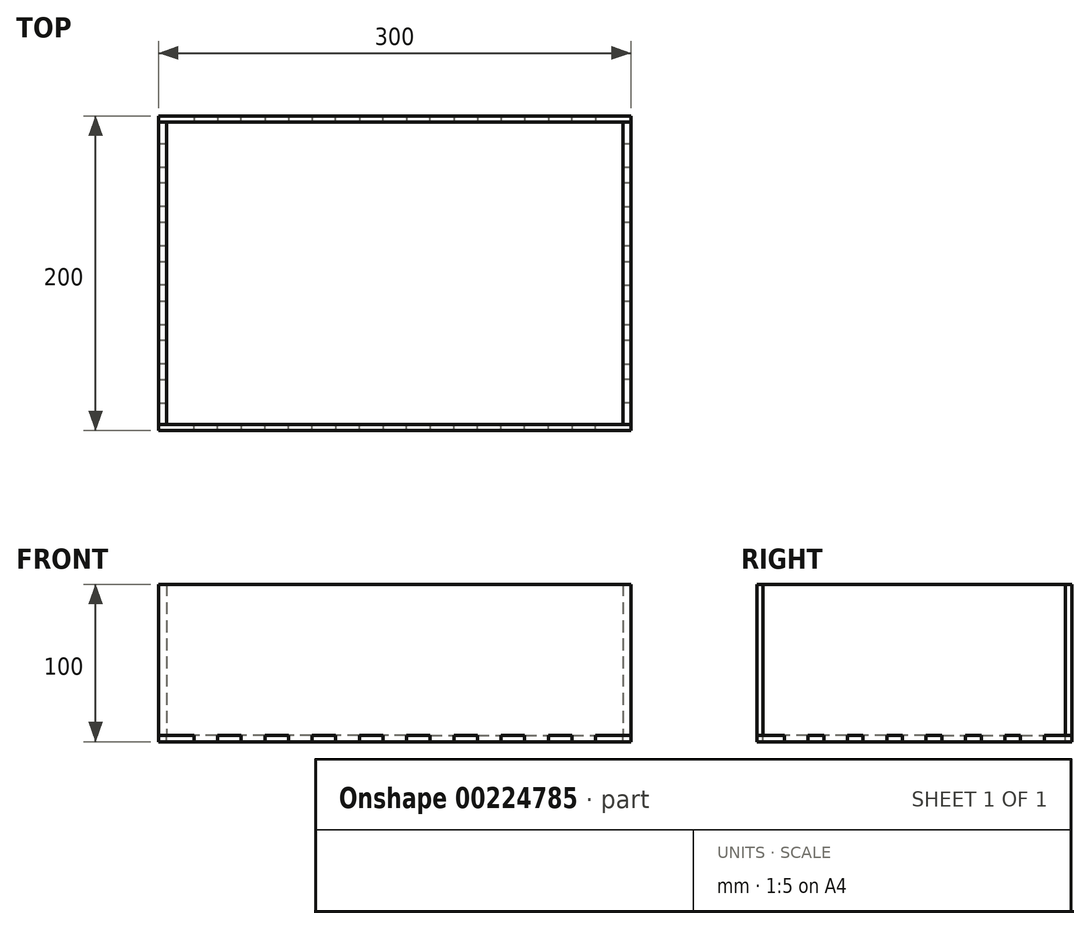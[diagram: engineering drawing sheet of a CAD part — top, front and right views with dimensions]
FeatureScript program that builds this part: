
annotation { "Feature Type Name" : "Feature", "Feature Type Description" : "" }
export const myFeature = defineFeature(function(context is Context, id is Id, definition is map)
    precondition{}
    {
        {
            var Q0;
            Q0=qCreatedBy(makeId("Top.planeOp"),FACE);
            var sketch = newSketch(context, id + "F0", { "sketchPlane" : qUnion([Q0])});
            skLineSegment(sketch, "E0.bottom", {"start": v(150, -100) * mm, "end": v(-150, -100) * mm});
            skLineSegment(sketch, "E0.top", {"start": v(150, 100) * mm, "end": v(-150, 100) * mm});
            skLineSegment(sketch, "E0.left", {"start": v(150, -100) * mm, "end": v(150, 100) * mm});
            skLineSegment(sketch, "E0.right", {"start": v(-150, -100) * mm, "end": v(-150, 100) * mm});
            skPoint(sketch, "E0.middle", {"position": v(0, 0) * mm});
            skLineSegment(sketch, "E1", {"start": v(0, 96) * mm, "end": v(7.5, 96) * mm});
            skLineSegment(sketch, "E2", {"start": v(7.5, 96) * mm, "end": v(7.5, 100) * mm});
            skLineSegment(sketch, "E3", {"start": v(0, 96) * mm, "end": v(-7.5, 96) * mm});
            skLineSegment(sketch, "E4", {"start": v(-7.5, 96) * mm, "end": v(-7.5, 100) * mm});
            skLineSegment(sketch, "E5", {"start": v(-7.5, 96) * mm, "end": v(7.5, 96) * mm});
            skPoint(sketch, "E6.start.orphan", {"position": v(0, 100) * mm});
            skLineSegment(sketch, "E7.1.0.0", {"start": v(22.5, 96) * mm, "end": v(22.5, 100) * mm});
            skLineSegment(sketch, "E7.1.0.1", {"start": v(22.5, 96) * mm, "end": v(37.5, 96) * mm});
            skLineSegment(sketch, "E7.1.0.2", {"start": v(37.5, 96) * mm, "end": v(37.5, 100) * mm});
            skLineSegment(sketch, "E7.2.0.0", {"start": v(52.5, 96) * mm, "end": v(52.5, 100) * mm});
            skLineSegment(sketch, "E7.2.0.1", {"start": v(52.5, 96) * mm, "end": v(67.5, 96) * mm});
            skLineSegment(sketch, "E7.2.0.2", {"start": v(67.5, 96) * mm, "end": v(67.5, 100) * mm});
            skLineSegment(sketch, "E7.3.0.0", {"start": v(82.5, 96) * mm, "end": v(82.5, 100) * mm});
            skLineSegment(sketch, "E7.3.0.1", {"start": v(82.5, 96) * mm, "end": v(97.5, 96) * mm});
            skLineSegment(sketch, "E7.3.0.2", {"start": v(97.5, 96) * mm, "end": v(97.5, 100) * mm});
            skLineSegment(sketch, "E7.4.0.0", {"start": v(112.5, 96) * mm, "end": v(112.5, 100) * mm});
            skLineSegment(sketch, "E7.4.0.1", {"start": v(112.5, 96) * mm, "end": v(127.5, 96) * mm});
            skLineSegment(sketch, "E7.4.0.2", {"start": v(127.5, 96) * mm, "end": v(127.5, 100) * mm});
            skLineSegment(sketch, "E7.direction1", {"start": v(-7.5, 96) * mm, "end": v(22.5, 96) * mm, "construction": true});
            skLineSegment(sketch, "E8.MirrorCS", {"start": v(-97.5, 96) * mm, "end": v(-97.5, 100) * mm});
            skLineSegment(sketch, "E9.MirrorCS", {"start": v(-67.5, 96) * mm, "end": v(-67.5, 100) * mm});
            skLineSegment(sketch, "E10.MirrorCS", {"start": v(-82.5, 96) * mm, "end": v(-82.5, 100) * mm});
            skLineSegment(sketch, "E11.MirrorCS", {"start": v(7.5, 96) * mm, "end": v(-7.5, 96) * mm});
            skLineSegment(sketch, "E12.MirrorCS", {"start": v(-22.5, 96) * mm, "end": v(-22.5, 100) * mm});
            skLineSegment(sketch, "E13.MirrorCS", {"start": v(-37.5, 96) * mm, "end": v(-37.5, 100) * mm});
            skLineSegment(sketch, "E14.MirrorCS", {"start": v(-52.5, 96) * mm, "end": v(-52.5, 100) * mm});
            skLineSegment(sketch, "E15.MirrorCS", {"start": v(-127.5, 96) * mm, "end": v(-127.5, 100) * mm});
            skLineSegment(sketch, "E16.MirrorCS", {"start": v(-112.5, 96) * mm, "end": v(-112.5, 100) * mm});
            skLineSegment(sketch, "E17.MirrorCS", {"start": v(-112.5, 96) * mm, "end": v(-127.5, 96) * mm});
            skLineSegment(sketch, "E18.MirrorCS", {"start": v(-52.5, 96) * mm, "end": v(-67.5, 96) * mm});
            skLineSegment(sketch, "E19.MirrorCS", {"start": v(7.5, 96) * mm, "end": v(-22.5, 96) * mm, "construction": true});
            skLineSegment(sketch, "E20.MirrorCS", {"start": v(-22.5, 96) * mm, "end": v(-37.5, 96) * mm});
            skLineSegment(sketch, "E21.MirrorCS", {"start": v(-82.5, 96) * mm, "end": v(-97.5, 96) * mm});
            skLineSegment(sketch, "E22.MirrorCS", {"start": v(0, -96) * mm, "end": v(-7.5, -96) * mm});
            skLineSegment(sketch, "E23.MirrorCS", {"start": v(0, -96) * mm, "end": v(7.5, -96) * mm});
            skLineSegment(sketch, "E24.MirrorCS", {"start": v(-7.5, -96) * mm, "end": v(7.5, -96) * mm});
            skLineSegment(sketch, "E25.MirrorCS", {"start": v(7.5, -96) * mm, "end": v(-7.5, -96) * mm});
            skLineSegment(sketch, "E26.MirrorCS", {"start": v(-7.5, -96) * mm, "end": v(-7.5, -100) * mm});
            skLineSegment(sketch, "E27.MirrorCS", {"start": v(7.5, -96) * mm, "end": v(7.5, -100) * mm});
            skLineSegment(sketch, "E28.MirrorCS", {"start": v(127.5, -96) * mm, "end": v(127.5, -100) * mm});
            skLineSegment(sketch, "E29.MirrorCS", {"start": v(52.5, -96) * mm, "end": v(52.5, -100) * mm});
            skLineSegment(sketch, "E30.MirrorCS", {"start": v(67.5, -96) * mm, "end": v(67.5, -100) * mm});
            skLineSegment(sketch, "E31.MirrorCS", {"start": v(82.5, -96) * mm, "end": v(82.5, -100) * mm});
            skLineSegment(sketch, "E32.MirrorCS", {"start": v(37.5, -96) * mm, "end": v(37.5, -100) * mm});
            skLineSegment(sketch, "E33.MirrorCS", {"start": v(-82.5, -96) * mm, "end": v(-82.5, -100) * mm});
            skLineSegment(sketch, "E34.MirrorCS", {"start": v(22.5, -96) * mm, "end": v(22.5, -100) * mm});
            skLineSegment(sketch, "E35.MirrorCS", {"start": v(-52.5, -96) * mm, "end": v(-52.5, -100) * mm});
            skPoint(sketch, "E36.MirrorP", {"position": v(0, -100) * mm});
            skLineSegment(sketch, "E37.MirrorCS", {"start": v(-97.5, -96) * mm, "end": v(-97.5, -100) * mm});
            skLineSegment(sketch, "E38.MirrorCS", {"start": v(-22.5, -96) * mm, "end": v(-22.5, -100) * mm});
            skLineSegment(sketch, "E39.MirrorCS", {"start": v(97.5, -96) * mm, "end": v(97.5, -100) * mm});
            skLineSegment(sketch, "E40.MirrorCS", {"start": v(-127.5, -96) * mm, "end": v(-127.5, -100) * mm});
            skLineSegment(sketch, "E41.MirrorCS", {"start": v(-67.5, -96) * mm, "end": v(-67.5, -100) * mm});
            skLineSegment(sketch, "E42.MirrorCS", {"start": v(-37.5, -96) * mm, "end": v(-37.5, -100) * mm});
            skLineSegment(sketch, "E43.MirrorCS", {"start": v(112.5, -96) * mm, "end": v(112.5, -100) * mm});
            skLineSegment(sketch, "E44.MirrorCS", {"start": v(-112.5, -96) * mm, "end": v(-112.5, -100) * mm});
            skLineSegment(sketch, "E45.MirrorCS", {"start": v(52.5, -96) * mm, "end": v(67.5, -96) * mm});
            skLineSegment(sketch, "E46.MirrorCS", {"start": v(-112.5, -96) * mm, "end": v(-127.5, -96) * mm});
            skLineSegment(sketch, "E47.MirrorCS", {"start": v(112.5, -96) * mm, "end": v(127.5, -96) * mm});
            skLineSegment(sketch, "E48.MirrorCS", {"start": v(-82.5, -96) * mm, "end": v(-97.5, -96) * mm});
            skLineSegment(sketch, "E49.MirrorCS", {"start": v(22.5, -96) * mm, "end": v(37.5, -96) * mm});
            skLineSegment(sketch, "E50.MirrorCS", {"start": v(-52.5, -96) * mm, "end": v(-67.5, -96) * mm});
            skLineSegment(sketch, "E51.MirrorCS", {"start": v(82.5, -96) * mm, "end": v(97.5, -96) * mm});
            skLineSegment(sketch, "E52.MirrorCS", {"start": v(-7.5, -96) * mm, "end": v(22.5, -96) * mm, "construction": true});
            skLineSegment(sketch, "E53.MirrorCS", {"start": v(7.5, -96) * mm, "end": v(-22.5, -96) * mm, "construction": true});
            skLineSegment(sketch, "E54.MirrorCS", {"start": v(-22.5, -96) * mm, "end": v(-37.5, -96) * mm});
            skLineSegment(sketch, "E55", {"start": v(-150, 0) * mm, "end": v(-146, 0) * mm});
            skPoint(sketch, "E55.endSnap0", {"position": v(-150, 0) * mm});
            skLineSegment(sketch, "E56", {"start": v(-145, 7.5) * mm, "end": v(-150, 7.5) * mm});
            skLineSegment(sketch, "E57", {"start": v(-145, -7.5) * mm, "end": v(-150, -7.5) * mm});
            skLineSegment(sketch, "E58", {"start": v(-145, -7.5) * mm, "end": v(-145, 7.5) * mm});
            skLineSegment(sketch, "E59.0.1.0", {"start": v(-145, 17.5) * mm, "end": v(-150, 17.5) * mm});
            skLineSegment(sketch, "E59.0.1.1", {"start": v(-145, 17.5) * mm, "end": v(-145, 32.5) * mm});
            skLineSegment(sketch, "E59.0.1.2", {"start": v(-145, 32.5) * mm, "end": v(-150, 32.5) * mm});
            skLineSegment(sketch, "E59.0.2.0", {"start": v(-145, 42.5) * mm, "end": v(-150, 42.5) * mm});
            skLineSegment(sketch, "E59.0.2.1", {"start": v(-145, 42.5) * mm, "end": v(-145, 57.5) * mm});
            skLineSegment(sketch, "E59.0.2.2", {"start": v(-145, 57.5) * mm, "end": v(-150, 57.5) * mm});
            skLineSegment(sketch, "E59.0.3.0", {"start": v(-145, 67.5) * mm, "end": v(-150, 67.5) * mm});
            skLineSegment(sketch, "E59.0.3.1", {"start": v(-145, 67.5) * mm, "end": v(-145, 82.5) * mm});
            skLineSegment(sketch, "E59.0.3.2", {"start": v(-145, 82.5) * mm, "end": v(-150, 82.5) * mm});
            skLineSegment(sketch, "E59.direction1", {"start": v(-150, -7.5) * mm, "end": v(-125, -7.5) * mm, "construction": true});
            skLineSegment(sketch, "E59.direction2", {"start": v(-150, -7.5) * mm, "end": v(-150, 17.5) * mm, "construction": true});
            skLineSegment(sketch, "E60.MirrorCS", {"start": v(-145, -17.5) * mm, "end": v(-150, -17.5) * mm});
            skLineSegment(sketch, "E61.MirrorCS", {"start": v(-145, -67.5) * mm, "end": v(-150, -67.5) * mm});
            skLineSegment(sketch, "E62.MirrorCS", {"start": v(-145, -57.5) * mm, "end": v(-150, -57.5) * mm});
            skLineSegment(sketch, "E63.MirrorCS", {"start": v(-145, -82.5) * mm, "end": v(-150, -82.5) * mm});
            skLineSegment(sketch, "E64.MirrorCS", {"start": v(-145, -42.5) * mm, "end": v(-150, -42.5) * mm});
            skLineSegment(sketch, "E65.MirrorCS", {"start": v(-145, -32.5) * mm, "end": v(-150, -32.5) * mm});
            skLineSegment(sketch, "E66.MirrorCS", {"start": v(-145, 7.5) * mm, "end": v(-145, -7.5) * mm});
            skLineSegment(sketch, "E67.MirrorCS", {"start": v(-145, -17.5) * mm, "end": v(-145, -32.5) * mm});
            skLineSegment(sketch, "E68.MirrorCS", {"start": v(-145, -67.5) * mm, "end": v(-145, -82.5) * mm});
            skLineSegment(sketch, "E69.MirrorCS", {"start": v(-150, 7.5) * mm, "end": v(-150, -17.5) * mm, "construction": true});
            skLineSegment(sketch, "E70.MirrorCS", {"start": v(-145, -42.5) * mm, "end": v(-145, -57.5) * mm});
            skLineSegment(sketch, "E71.MirrorCS", {"start": v(145, -7.5) * mm, "end": v(150, -7.5) * mm});
            skLineSegment(sketch, "E72.MirrorCS", {"start": v(145, 7.5) * mm, "end": v(150, 7.5) * mm});
            skLineSegment(sketch, "E73.MirrorCS", {"start": v(145, 7.5) * mm, "end": v(145, -7.5) * mm});
            skLineSegment(sketch, "E74.MirrorCS", {"start": v(150, 0) * mm, "end": v(146, 0) * mm});
            skLineSegment(sketch, "E75.MirrorCS", {"start": v(145, -7.5) * mm, "end": v(145, 7.5) * mm});
            skLineSegment(sketch, "E76.MirrorCS", {"start": v(145, -17.5) * mm, "end": v(150, -17.5) * mm});
            skLineSegment(sketch, "E77.MirrorCS", {"start": v(145, 17.5) * mm, "end": v(150, 17.5) * mm});
            skLineSegment(sketch, "E78.MirrorCS", {"start": v(145, 57.5) * mm, "end": v(150, 57.5) * mm});
            skLineSegment(sketch, "E79.MirrorCS", {"start": v(145, 67.5) * mm, "end": v(150, 67.5) * mm});
            skLineSegment(sketch, "E80.MirrorCS", {"start": v(145, -67.5) * mm, "end": v(150, -67.5) * mm});
            skLineSegment(sketch, "E81.MirrorCS", {"start": v(145, 82.5) * mm, "end": v(150, 82.5) * mm});
            skLineSegment(sketch, "E82.MirrorCS", {"start": v(145, -57.5) * mm, "end": v(150, -57.5) * mm});
            skPoint(sketch, "E83.MirrorP", {"position": v(150, 0) * mm});
            skLineSegment(sketch, "E84.MirrorCS", {"start": v(145, 42.5) * mm, "end": v(150, 42.5) * mm});
            skLineSegment(sketch, "E85.MirrorCS", {"start": v(145, -32.5) * mm, "end": v(150, -32.5) * mm});
            skLineSegment(sketch, "E86.MirrorCS", {"start": v(145, 32.5) * mm, "end": v(150, 32.5) * mm});
            skLineSegment(sketch, "E87.MirrorCS", {"start": v(145, -42.5) * mm, "end": v(150, -42.5) * mm});
            skLineSegment(sketch, "E88.MirrorCS", {"start": v(145, -82.5) * mm, "end": v(150, -82.5) * mm});
            skLineSegment(sketch, "E89.MirrorCS", {"start": v(145, -42.5) * mm, "end": v(145, -57.5) * mm});
            skLineSegment(sketch, "E90.MirrorCS", {"start": v(145, -17.5) * mm, "end": v(145, -32.5) * mm});
            skLineSegment(sketch, "E91.MirrorCS", {"start": v(145, 42.5) * mm, "end": v(145, 57.5) * mm});
            skLineSegment(sketch, "E92.MirrorCS", {"start": v(145, -67.5) * mm, "end": v(145, -82.5) * mm});
            skLineSegment(sketch, "E93.MirrorCS", {"start": v(150, 7.5) * mm, "end": v(150, -17.5) * mm, "construction": true});
            skLineSegment(sketch, "E94.MirrorCS", {"start": v(145, 67.5) * mm, "end": v(145, 82.5) * mm});
            skLineSegment(sketch, "E95.MirrorCS", {"start": v(150, -7.5) * mm, "end": v(150, 17.5) * mm, "construction": true});
            skLineSegment(sketch, "E96.MirrorCS", {"start": v(145, 17.5) * mm, "end": v(145, 32.5) * mm});
            skSolve(sketch);
        }
        {
            var Q0;
            {var subQ54=sQuery(id+"F0.wireOp",EDGE,"E7.1.0.0");Q0=makeQuery(id+"F0.imprint","IMPRINT",FACE,{"disambiguationData":[TD([[makeQuery(id+"F0.imprint","IMPRINT",EDGE,{"derivedFrom":subQ54}),1.0]])]});}
            extrude(context, id + "F1", {"entities" : qUnion([Q0]), "depth" : 4 * mm});
        }
        {
            var Q0;
            Q0=makeQuery(id+"F1.opExtrude","CAP_FACE",FACE,{"disambiguationData":[OSD([sQuery(id+"F0.wireOp",EDGE,"E0.bottom"),sQuery(id+"F0.wireOp",EDGE,"E0.top"),sQuery(id+"F0.wireOp",EDGE,"E0.left"),sQuery(id+"F0.wireOp",EDGE,"E0.right"),sQuery(id+"F0.wireOp",EDGE,"E7.1.0.0"),sQuery(id+"F0.wireOp",EDGE,"E7.1.0.1"),sQuery(id+"F0.wireOp",EDGE,"E7.1.0.2"),sQuery(id+"F0.wireOp",EDGE,"E7.2.0.0"),sQuery(id+"F0.wireOp",EDGE,"E7.2.0.1"),sQuery(id+"F0.wireOp",EDGE,"E7.2.0.2"),sQuery(id+"F0.wireOp",EDGE,"E7.3.0.0"),sQuery(id+"F0.wireOp",EDGE,"E7.3.0.1"),sQuery(id+"F0.wireOp",EDGE,"E7.3.0.2"),sQuery(id+"F0.wireOp",EDGE,"E7.4.0.0"),sQuery(id+"F0.wireOp",EDGE,"E7.4.0.1"),sQuery(id+"F0.wireOp",EDGE,"E7.4.0.2"),sQuery(id+"F0.wireOp",EDGE,"E8.MirrorCS"),sQuery(id+"F0.wireOp",EDGE,"E9.MirrorCS"),sQuery(id+"F0.wireOp",EDGE,"E10.MirrorCS"),sQuery(id+"F0.wireOp",EDGE,"E4"),sQuery(id+"F0.wireOp",EDGE,"E2"),sQuery(id+"F0.wireOp",EDGE,"E11.MirrorCS"),sQuery(id+"F0.wireOp",EDGE,"E12.MirrorCS"),sQuery(id+"F0.wireOp",EDGE,"E13.MirrorCS"),sQuery(id+"F0.wireOp",EDGE,"E14.MirrorCS"),sQuery(id+"F0.wireOp",EDGE,"E15.MirrorCS"),sQuery(id+"F0.wireOp",EDGE,"E16.MirrorCS"),sQuery(id+"F0.wireOp",EDGE,"E17.MirrorCS"),sQuery(id+"F0.wireOp",EDGE,"E18.MirrorCS"),sQuery(id+"F0.wireOp",EDGE,"E20.MirrorCS"),sQuery(id+"F0.wireOp",EDGE,"E21.MirrorCS"),sQuery(id+"F0.wireOp",EDGE,"E25.MirrorCS"),sQuery(id+"F0.wireOp",EDGE,"E22.MirrorCS"),sQuery(id+"F0.wireOp",EDGE,"E26.MirrorCS"),sQuery(id+"F0.wireOp",EDGE,"E27.MirrorCS"),sQuery(id+"F0.wireOp",EDGE,"E28.MirrorCS"),sQuery(id+"F0.wireOp",EDGE,"E29.MirrorCS"),sQuery(id+"F0.wireOp",EDGE,"E30.MirrorCS"),sQuery(id+"F0.wireOp",EDGE,"E31.MirrorCS"),sQuery(id+"F0.wireOp",EDGE,"E32.MirrorCS"),sQuery(id+"F0.wireOp",EDGE,"E33.MirrorCS"),sQuery(id+"F0.wireOp",EDGE,"E34.MirrorCS"),sQuery(id+"F0.wireOp",EDGE,"E35.MirrorCS"),sQuery(id+"F0.wireOp",EDGE,"E37.MirrorCS"),sQuery(id+"F0.wireOp",EDGE,"E38.MirrorCS"),sQuery(id+"F0.wireOp",EDGE,"E39.MirrorCS"),sQuery(id+"F0.wireOp",EDGE,"E40.MirrorCS"),sQuery(id+"F0.wireOp",EDGE,"E41.MirrorCS"),sQuery(id+"F0.wireOp",EDGE,"E42.MirrorCS"),sQuery(id+"F0.wireOp",EDGE,"E43.MirrorCS"),sQuery(id+"F0.wireOp",EDGE,"E44.MirrorCS"),sQuery(id+"F0.wireOp",EDGE,"E45.MirrorCS"),sQuery(id+"F0.wireOp",EDGE,"E46.MirrorCS"),sQuery(id+"F0.wireOp",EDGE,"E47.MirrorCS"),sQuery(id+"F0.wireOp",EDGE,"E48.MirrorCS"),sQuery(id+"F0.wireOp",EDGE,"E49.MirrorCS"),sQuery(id+"F0.wireOp",EDGE,"E50.MirrorCS"),sQuery(id+"F0.wireOp",EDGE,"E51.MirrorCS"),sQuery(id+"F0.wireOp",EDGE,"E54.MirrorCS"),sQuery(id+"F0.wireOp",EDGE,"E59.0.1.0"),sQuery(id+"F0.wireOp",EDGE,"E59.0.1.1"),sQuery(id+"F0.wireOp",EDGE,"E59.0.1.2"),sQuery(id+"F0.wireOp",EDGE,"E59.0.2.0"),sQuery(id+"F0.wireOp",EDGE,"E59.0.2.1"),sQuery(id+"F0.wireOp",EDGE,"E59.0.2.2"),sQuery(id+"F0.wireOp",EDGE,"E59.0.3.0"),sQuery(id+"F0.wireOp",EDGE,"E59.0.3.1"),sQuery(id+"F0.wireOp",EDGE,"E59.0.3.2"),sQuery(id+"F0.wireOp",EDGE,"E60.MirrorCS"),sQuery(id+"F0.wireOp",EDGE,"E56"),sQuery(id+"F0.wireOp",EDGE,"E61.MirrorCS"),sQuery(id+"F0.wireOp",EDGE,"E62.MirrorCS"),sQuery(id+"F0.wireOp",EDGE,"E57"),sQuery(id+"F0.wireOp",EDGE,"E63.MirrorCS"),sQuery(id+"F0.wireOp",EDGE,"E64.MirrorCS"),sQuery(id+"F0.wireOp",EDGE,"E65.MirrorCS"),sQuery(id+"F0.wireOp",EDGE,"E66.MirrorCS"),sQuery(id+"F0.wireOp",EDGE,"E67.MirrorCS"),sQuery(id+"F0.wireOp",EDGE,"E68.MirrorCS"),sQuery(id+"F0.wireOp",EDGE,"E70.MirrorCS"),sQuery(id+"F0.wireOp",EDGE,"E71.MirrorCS"),sQuery(id+"F0.wireOp",EDGE,"E72.MirrorCS"),sQuery(id+"F0.wireOp",EDGE,"E75.MirrorCS"),sQuery(id+"F0.wireOp",EDGE,"E76.MirrorCS"),sQuery(id+"F0.wireOp",EDGE,"E77.MirrorCS"),sQuery(id+"F0.wireOp",EDGE,"E78.MirrorCS"),sQuery(id+"F0.wireOp",EDGE,"E79.MirrorCS"),sQuery(id+"F0.wireOp",EDGE,"E80.MirrorCS"),sQuery(id+"F0.wireOp",EDGE,"E81.MirrorCS"),sQuery(id+"F0.wireOp",EDGE,"E82.MirrorCS"),sQuery(id+"F0.wireOp",EDGE,"E84.MirrorCS"),sQuery(id+"F0.wireOp",EDGE,"E85.MirrorCS"),sQuery(id+"F0.wireOp",EDGE,"E86.MirrorCS"),sQuery(id+"F0.wireOp",EDGE,"E87.MirrorCS"),sQuery(id+"F0.wireOp",EDGE,"E88.MirrorCS"),sQuery(id+"F0.wireOp",EDGE,"E89.MirrorCS"),sQuery(id+"F0.wireOp",EDGE,"E90.MirrorCS"),sQuery(id+"F0.wireOp",EDGE,"E91.MirrorCS"),sQuery(id+"F0.wireOp",EDGE,"E92.MirrorCS"),sQuery(id+"F0.wireOp",EDGE,"E94.MirrorCS"),sQuery(id+"F0.wireOp",EDGE,"E96.MirrorCS")])],"isStart":false});
            var sketch = newSketch(context, id + "F2", { "sketchPlane" : qUnion([Q0])});
            skLineSegment(sketch, "E97.2", {"start": v(-82.5, 96) * mm, "end": v(-82.5, 100) * mm});
            skLineSegment(sketch, "E97.4", {"start": v(-112.5, 96) * mm, "end": v(-112.5, 100) * mm});
            skLineSegment(sketch, "E97.6", {"start": v(82.5, 96) * mm, "end": v(82.5, 100) * mm});
            skLineSegment(sketch, "E97.7", {"start": v(-97.5, 100) * mm, "end": v(-112.5, 100) * mm});
            skLineSegment(sketch, "E97.10", {"start": v(-97.5, 96) * mm, "end": v(-97.5, 100) * mm});
            skLineSegment(sketch, "E97.11", {"start": v(-52.5, 96) * mm, "end": v(-52.5, 100) * mm});
            skLineSegment(sketch, "E97.12", {"start": v(-7.5, 96) * mm, "end": v(-7.5, 100) * mm});
            skLineSegment(sketch, "E97.13", {"start": v(82.5, 96) * mm, "end": v(97.5, 96) * mm});
            skLineSegment(sketch, "E97.14", {"start": v(52.5, 96) * mm, "end": v(52.5, 100) * mm});
            skLineSegment(sketch, "E97.16", {"start": v(-37.5, 96) * mm, "end": v(-37.5, 100) * mm});
            skLineSegment(sketch, "E97.19", {"start": v(-112.5, 96) * mm, "end": v(-127.5, 96) * mm});
            skLineSegment(sketch, "E97.20", {"start": v(-127.5, 96) * mm, "end": v(-127.5, 100) * mm});
            skLineSegment(sketch, "E97.21", {"start": v(67.5, 96) * mm, "end": v(67.5, 100) * mm});
            skLineSegment(sketch, "E97.22", {"start": v(-67.5, 96) * mm, "end": v(-67.5, 100) * mm});
            skLineSegment(sketch, "E97.24", {"start": v(22.5, 96) * mm, "end": v(22.5, 100) * mm});
            skLineSegment(sketch, "E97.25", {"start": v(97.5, 96) * mm, "end": v(97.5, 100) * mm});
            skLineSegment(sketch, "E97.26", {"start": v(7.5, 96) * mm, "end": v(7.5, 100) * mm});
            skLineSegment(sketch, "E97.27", {"start": v(-52.5, 96) * mm, "end": v(-67.5, 96) * mm});
            skLineSegment(sketch, "E97.29", {"start": v(37.5, 96) * mm, "end": v(37.5, 100) * mm});
            skLineSegment(sketch, "E97.30", {"start": v(112.5, 96) * mm, "end": v(127.5, 96) * mm});
            skLineSegment(sketch, "E97.31", {"start": v(52.5, 100) * mm, "end": v(37.5, 100) * mm});
            skLineSegment(sketch, "E97.32", {"start": v(22.5, 96) * mm, "end": v(37.5, 96) * mm});
            skLineSegment(sketch, "E97.33", {"start": v(112.5, 96) * mm, "end": v(112.5, 100) * mm});
            skLineSegment(sketch, "E97.34", {"start": v(127.5, 96) * mm, "end": v(127.5, 100) * mm});
            skLineSegment(sketch, "E97.35", {"start": v(52.5, 96) * mm, "end": v(67.5, 96) * mm});
            skLineSegment(sketch, "E97.36", {"start": v(7.5, 96) * mm, "end": v(-7.5, 96) * mm});
            skLineSegment(sketch, "E97.37", {"start": v(-22.5, 96) * mm, "end": v(-37.5, 96) * mm});
            skLineSegment(sketch, "E97.38", {"start": v(22.5, 100) * mm, "end": v(7.5, 100) * mm});
            skLineSegment(sketch, "E97.39", {"start": v(-22.5, 96) * mm, "end": v(-22.5, 100) * mm});
            skLineSegment(sketch, "E97.40", {"start": v(-82.5, 96) * mm, "end": v(-97.5, 96) * mm});
            skLineSegment(sketch, "E97.42", {"start": v(67.5, 96) * mm, "end": v(67.5, 100) * mm});
            skLineSegment(sketch, "E97.43", {"start": v(-97.5, 96) * mm, "end": v(-97.5, 100) * mm});
            skLineSegment(sketch, "E97.47", {"start": v(-67.5, 96) * mm, "end": v(-67.5, 100) * mm});
            skLineSegment(sketch, "E97.48", {"start": v(82.5, 96) * mm, "end": v(82.5, 100) * mm});
            skLineSegment(sketch, "E97.50", {"start": v(52.5, 96) * mm, "end": v(67.5, 96) * mm});
            skLineSegment(sketch, "E97.55", {"start": v(-67.5, 100) * mm, "end": v(-82.5, 100) * mm});
            skLineSegment(sketch, "E97.56", {"start": v(-7.5, 96) * mm, "end": v(-7.5, 100) * mm});
            skLineSegment(sketch, "E97.57", {"start": v(82.5, 96) * mm, "end": v(97.5, 96) * mm});
            skLineSegment(sketch, "E97.58", {"start": v(112.5, 100) * mm, "end": v(97.5, 100) * mm});
            skLineSegment(sketch, "E97.59", {"start": v(-112.5, 96) * mm, "end": v(-127.5, 96) * mm});
            skLineSegment(sketch, "E97.60", {"start": v(-127.5, 96) * mm, "end": v(-127.5, 100) * mm});
            skLineSegment(sketch, "E97.61", {"start": v(-52.5, 96) * mm, "end": v(-67.5, 96) * mm});
            skLineSegment(sketch, "E97.64", {"start": v(97.5, 96) * mm, "end": v(97.5, 100) * mm});
            skLineSegment(sketch, "E97.71", {"start": v(82.5, 100) * mm, "end": v(67.5, 100) * mm});
            skLineSegment(sketch, "E97.72", {"start": v(22.5, 96) * mm, "end": v(22.5, 100) * mm});
            skLineSegment(sketch, "E97.74", {"start": v(-82.5, 96) * mm, "end": v(-82.5, 100) * mm});
            skLineSegment(sketch, "E97.75", {"start": v(-112.5, 96) * mm, "end": v(-112.5, 100) * mm});
            skLineSegment(sketch, "E97.78", {"start": v(22.5, 96) * mm, "end": v(37.5, 96) * mm});
            skLineSegment(sketch, "E97.79", {"start": v(112.5, 96) * mm, "end": v(112.5, 100) * mm});
            skLineSegment(sketch, "E97.80", {"start": v(7.5, 96) * mm, "end": v(-7.5, 96) * mm});
            skLineSegment(sketch, "E97.81", {"start": v(-22.5, 96) * mm, "end": v(-37.5, 96) * mm});
            skLineSegment(sketch, "E97.84", {"start": v(22.5, 100) * mm, "end": v(7.5, 100) * mm});
            skLineSegment(sketch, "E97.85", {"start": v(37.5, 96) * mm, "end": v(37.5, 100) * mm});
            skLineSegment(sketch, "E97.86", {"start": v(112.5, 96) * mm, "end": v(127.5, 96) * mm});
            skLineSegment(sketch, "E97.87", {"start": v(-82.5, 96) * mm, "end": v(-97.5, 96) * mm});
            skLineSegment(sketch, "E97.90", {"start": v(-37.5, 96) * mm, "end": v(-37.5, 100) * mm});
            skLineSegment(sketch, "E97.91", {"start": v(52.5, 96) * mm, "end": v(52.5, 100) * mm});
            skLineSegment(sketch, "E97.92", {"start": v(127.5, 96) * mm, "end": v(127.5, 100) * mm});
            skLineSegment(sketch, "E97.95", {"start": v(-7.5, 100) * mm, "end": v(-22.5, 100) * mm});
            skLineSegment(sketch, "E97.98", {"start": v(-52.5, 96) * mm, "end": v(-52.5, 100) * mm});
            skLineSegment(sketch, "E97.99", {"start": v(-37.5, 100) * mm, "end": v(-52.5, 100) * mm});
            skLineSegment(sketch, "E97.100", {"start": v(7.5, 96) * mm, "end": v(7.5, 100) * mm});
            skLineSegment(sketch, "E97.104", {"start": v(-22.5, 96) * mm, "end": v(-22.5, 100) * mm});
            skLineSegment(sketch, "E98", {"start": v(-127.5, 100) * mm, "end": v(-112.5, 100) * mm});
            skLineSegment(sketch, "E99.trimOffspring", {"start": v(-7.5, 100) * mm, "end": v(7.5, 100) * mm});
            skLineSegment(sketch, "E100.trimOffspring", {"start": v(-37.5, 100) * mm, "end": v(-22.5, 100) * mm});
            skLineSegment(sketch, "E101.trimOffspring", {"start": v(-97.5, 100) * mm, "end": v(-82.5, 100) * mm});
            skLineSegment(sketch, "E102.trimOffspring", {"start": v(-67.5, 100) * mm, "end": v(-52.5, 100) * mm});
            skLineSegment(sketch, "E103.trimOffspring", {"start": v(22.5, 100) * mm, "end": v(127.5, 100) * mm});
            skLineSegment(sketch, "E104.MirrorCS", {"start": v(-97.5, -96) * mm, "end": v(-97.5, -100) * mm});
            skLineSegment(sketch, "E105.MirrorCS", {"start": v(-112.5, -96) * mm, "end": v(-112.5, -100) * mm});
            skLineSegment(sketch, "E106.MirrorCS", {"start": v(7.5, -96) * mm, "end": v(7.5, -100) * mm});
            skLineSegment(sketch, "E107.MirrorCS", {"start": v(22.5, -96) * mm, "end": v(22.5, -100) * mm});
            skLineSegment(sketch, "E108.MirrorCS", {"start": v(-52.5, -96) * mm, "end": v(-52.5, -100) * mm});
            skLineSegment(sketch, "E109.MirrorCS", {"start": v(-7.5, -96) * mm, "end": v(-7.5, -100) * mm});
            skLineSegment(sketch, "E110.MirrorCS", {"start": v(-67.5, -96) * mm, "end": v(-67.5, -100) * mm});
            skLineSegment(sketch, "E111.MirrorCS", {"start": v(-22.5, -96) * mm, "end": v(-22.5, -100) * mm});
            skLineSegment(sketch, "E112.MirrorCS", {"start": v(-37.5, -96) * mm, "end": v(-37.5, -100) * mm});
            skLineSegment(sketch, "E113.MirrorCS", {"start": v(-82.5, -96) * mm, "end": v(-82.5, -100) * mm});
            skLineSegment(sketch, "E114.MirrorCS", {"start": v(37.5, -96) * mm, "end": v(37.5, -100) * mm});
            skLineSegment(sketch, "E115.MirrorCS", {"start": v(52.5, -96) * mm, "end": v(52.5, -100) * mm});
            skLineSegment(sketch, "E116.MirrorCS", {"start": v(97.5, -96) * mm, "end": v(97.5, -100) * mm});
            skLineSegment(sketch, "E117.MirrorCS", {"start": v(-127.5, -96) * mm, "end": v(-127.5, -100) * mm});
            skLineSegment(sketch, "E118.MirrorCS", {"start": v(82.5, -96) * mm, "end": v(82.5, -100) * mm});
            skLineSegment(sketch, "E119.MirrorCS", {"start": v(127.5, -96) * mm, "end": v(127.5, -100) * mm});
            skLineSegment(sketch, "E120.MirrorCS", {"start": v(112.5, -96) * mm, "end": v(112.5, -100) * mm});
            skLineSegment(sketch, "E121.MirrorCS", {"start": v(67.5, -96) * mm, "end": v(67.5, -100) * mm});
            skLineSegment(sketch, "E122.MirrorCS", {"start": v(-112.5, -96) * mm, "end": v(-127.5, -96) * mm});
            skLineSegment(sketch, "E123.MirrorCS", {"start": v(22.5, -96) * mm, "end": v(37.5, -96) * mm});
            skLineSegment(sketch, "E124.MirrorCS", {"start": v(82.5, -96) * mm, "end": v(97.5, -96) * mm});
            skLineSegment(sketch, "E125.MirrorCS", {"start": v(-82.5, -96) * mm, "end": v(-97.5, -96) * mm});
            skLineSegment(sketch, "E126.MirrorCS", {"start": v(7.5, -96) * mm, "end": v(-7.5, -96) * mm});
            skLineSegment(sketch, "E127.MirrorCS", {"start": v(112.5, -96) * mm, "end": v(127.5, -96) * mm});
            skLineSegment(sketch, "E128.MirrorCS", {"start": v(-52.5, -96) * mm, "end": v(-67.5, -96) * mm});
            skLineSegment(sketch, "E129.MirrorCS", {"start": v(-22.5, -96) * mm, "end": v(-37.5, -96) * mm});
            skLineSegment(sketch, "E130.MirrorCS", {"start": v(82.5, -100) * mm, "end": v(67.5, -100) * mm});
            skLineSegment(sketch, "E131.MirrorCS", {"start": v(52.5, -100) * mm, "end": v(37.5, -100) * mm});
            skLineSegment(sketch, "E132.MirrorCS", {"start": v(22.5, -100) * mm, "end": v(7.5, -100) * mm});
            skLineSegment(sketch, "E133.MirrorCS", {"start": v(52.5, -96) * mm, "end": v(67.5, -96) * mm});
            skLineSegment(sketch, "E134.MirrorCS", {"start": v(-7.5, -100) * mm, "end": v(7.5, -100) * mm});
            skLineSegment(sketch, "E135.MirrorCS", {"start": v(-127.5, -100) * mm, "end": v(-112.5, -100) * mm});
            skLineSegment(sketch, "E136.MirrorCS", {"start": v(112.5, -100) * mm, "end": v(97.5, -100) * mm});
            skLineSegment(sketch, "E137.MirrorCS", {"start": v(-67.5, -100) * mm, "end": v(-52.5, -100) * mm});
            skLineSegment(sketch, "E138.MirrorCS", {"start": v(-67.5, -100) * mm, "end": v(-82.5, -100) * mm});
            skLineSegment(sketch, "E139.MirrorCS", {"start": v(-7.5, -100) * mm, "end": v(-22.5, -100) * mm});
            skLineSegment(sketch, "E140.MirrorCS", {"start": v(22.5, -100) * mm, "end": v(127.5, -100) * mm});
            skLineSegment(sketch, "E141.MirrorCS", {"start": v(-37.5, -100) * mm, "end": v(-52.5, -100) * mm});
            skLineSegment(sketch, "E142.MirrorCS", {"start": v(-37.5, -100) * mm, "end": v(-22.5, -100) * mm});
            skLineSegment(sketch, "E143.MirrorCS", {"start": v(-97.5, -100) * mm, "end": v(-112.5, -100) * mm});
            skLineSegment(sketch, "E144.MirrorCS", {"start": v(-97.5, -100) * mm, "end": v(-82.5, -100) * mm});
            skLineSegment(sketch, "E145.0", {"start": v(-150, -17.5) * mm, "end": v(-150, -7.5) * mm});
            skLineSegment(sketch, "E145.1", {"start": v(-150, 57.5) * mm, "end": v(-150, 67.5) * mm});
            skLineSegment(sketch, "E145.2", {"start": v(-145, -32.5) * mm, "end": v(-150, -32.5) * mm});
            skLineSegment(sketch, "E145.3", {"start": v(-145, 17.5) * mm, "end": v(-150, 17.5) * mm});
            skLineSegment(sketch, "E145.4", {"start": v(-145, 82.5) * mm, "end": v(-150, 82.5) * mm});
            skLineSegment(sketch, "E145.5", {"start": v(-150, 7.5) * mm, "end": v(-150, 17.5) * mm});
            skLineSegment(sketch, "E145.6", {"start": v(-145, -17.5) * mm, "end": v(-150, -17.5) * mm});
            skLineSegment(sketch, "E145.7", {"start": v(-145, 7.5) * mm, "end": v(-145, -7.5) * mm});
            skLineSegment(sketch, "E145.8", {"start": v(-145, 67.5) * mm, "end": v(-150, 67.5) * mm});
            skLineSegment(sketch, "E145.9", {"start": v(-145, -82.5) * mm, "end": v(-150, -82.5) * mm});
            skLineSegment(sketch, "E145.10", {"start": v(-145, 57.5) * mm, "end": v(-150, 57.5) * mm});
            skLineSegment(sketch, "E145.11", {"start": v(-145, 17.5) * mm, "end": v(-145, 32.5) * mm});
            skLineSegment(sketch, "E145.12", {"start": v(-150, 32.5) * mm, "end": v(-150, 42.5) * mm});
            skLineSegment(sketch, "E145.13", {"start": v(-145, 67.5) * mm, "end": v(-145, 82.5) * mm});
            skLineSegment(sketch, "E145.14", {"start": v(-145, -42.5) * mm, "end": v(-150, -42.5) * mm});
            skLineSegment(sketch, "E145.15", {"start": v(-145, 7.5) * mm, "end": v(-150, 7.5) * mm});
            skLineSegment(sketch, "E145.16", {"start": v(-145, -17.5) * mm, "end": v(-145, -32.5) * mm});
            skLineSegment(sketch, "E145.17", {"start": v(-145, 32.5) * mm, "end": v(-150, 32.5) * mm});
            skLineSegment(sketch, "E145.18", {"start": v(-150, -42.5) * mm, "end": v(-150, -32.5) * mm});
            skLineSegment(sketch, "E145.19", {"start": v(-150, -67.5) * mm, "end": v(-150, -57.5) * mm});
            skLineSegment(sketch, "E145.20", {"start": v(-145, -42.5) * mm, "end": v(-145, -57.5) * mm});
            skLineSegment(sketch, "E145.21", {"start": v(-145, 42.5) * mm, "end": v(-145, 57.5) * mm});
            skLineSegment(sketch, "E145.22", {"start": v(-145, -57.5) * mm, "end": v(-150, -57.5) * mm});
            skLineSegment(sketch, "E145.23", {"start": v(-145, -7.5) * mm, "end": v(-150, -7.5) * mm});
            skLineSegment(sketch, "E145.24", {"start": v(-145, -67.5) * mm, "end": v(-145, -82.5) * mm});
            skLineSegment(sketch, "E145.25", {"start": v(-145, -67.5) * mm, "end": v(-150, -67.5) * mm});
            skLineSegment(sketch, "E145.26", {"start": v(-145, 42.5) * mm, "end": v(-150, 42.5) * mm});
            skLineSegment(sketch, "E145.30", {"start": v(-150, 32.5) * mm, "end": v(-150, 42.5) * mm});
            skLineSegment(sketch, "E145.32", {"start": v(-145, 82.5) * mm, "end": v(-150, 82.5) * mm});
            skLineSegment(sketch, "E145.33", {"start": v(-145, 67.5) * mm, "end": v(-150, 67.5) * mm});
            skLineSegment(sketch, "E145.34", {"start": v(-145, -17.5) * mm, "end": v(-150, -17.5) * mm});
            skLineSegment(sketch, "E145.35", {"start": v(-145, 17.5) * mm, "end": v(-145, 32.5) * mm});
            skLineSegment(sketch, "E145.37", {"start": v(-145, -82.5) * mm, "end": v(-150, -82.5) * mm});
            skLineSegment(sketch, "E145.42", {"start": v(-150, 57.5) * mm, "end": v(-150, 67.5) * mm});
            skLineSegment(sketch, "E145.44", {"start": v(-145, 17.5) * mm, "end": v(-150, 17.5) * mm});
            skLineSegment(sketch, "E145.45", {"start": v(-145, 32.5) * mm, "end": v(-150, 32.5) * mm});
            skLineSegment(sketch, "E145.47", {"start": v(-145, 7.5) * mm, "end": v(-145, -7.5) * mm});
            skLineSegment(sketch, "E145.49", {"start": v(-145, -17.5) * mm, "end": v(-145, -32.5) * mm});
            skLineSegment(sketch, "E145.51", {"start": v(-145, 7.5) * mm, "end": v(-150, 7.5) * mm});
            skLineSegment(sketch, "E145.53", {"start": v(-145, -32.5) * mm, "end": v(-150, -32.5) * mm});
            skLineSegment(sketch, "E145.54", {"start": v(-145, 42.5) * mm, "end": v(-150, 42.5) * mm});
            skLineSegment(sketch, "E145.55", {"start": v(-145, -67.5) * mm, "end": v(-150, -67.5) * mm});
            skLineSegment(sketch, "E145.60", {"start": v(-150, -67.5) * mm, "end": v(-150, -57.5) * mm});
            skLineSegment(sketch, "E145.61", {"start": v(-145, -67.5) * mm, "end": v(-145, -82.5) * mm});
            skLineSegment(sketch, "E145.62", {"start": v(-145, 42.5) * mm, "end": v(-145, 57.5) * mm});
            skLineSegment(sketch, "E145.65", {"start": v(-145, 57.5) * mm, "end": v(-150, 57.5) * mm});
            skLineSegment(sketch, "E145.66", {"start": v(-145, -7.5) * mm, "end": v(-150, -7.5) * mm});
            skLineSegment(sketch, "E145.67", {"start": v(-150, -17.5) * mm, "end": v(-150, -7.5) * mm});
            skLineSegment(sketch, "E145.72", {"start": v(-150, 7.5) * mm, "end": v(-150, 17.5) * mm});
            skLineSegment(sketch, "E145.75", {"start": v(-145, -42.5) * mm, "end": v(-150, -42.5) * mm});
            skLineSegment(sketch, "E145.76", {"start": v(-145, 67.5) * mm, "end": v(-145, 82.5) * mm});
            skLineSegment(sketch, "E145.77", {"start": v(-150, -42.5) * mm, "end": v(-150, -32.5) * mm});
            skLineSegment(sketch, "E145.80", {"start": v(-145, -42.5) * mm, "end": v(-145, -57.5) * mm});
            skLineSegment(sketch, "E145.81", {"start": v(-145, -57.5) * mm, "end": v(-150, -57.5) * mm});
            skLineSegment(sketch, "E146", {"start": v(-150, 82.5) * mm, "end": v(-150, -82.5) * mm});
            skLineSegment(sketch, "E147.MirrorCS", {"start": v(145, -42.5) * mm, "end": v(150, -42.5) * mm});
            skLineSegment(sketch, "E148.MirrorCS", {"start": v(145, 32.5) * mm, "end": v(150, 32.5) * mm});
            skLineSegment(sketch, "E149.MirrorCS", {"start": v(145, 17.5) * mm, "end": v(150, 17.5) * mm});
            skLineSegment(sketch, "E150.MirrorCS", {"start": v(145, -32.5) * mm, "end": v(150, -32.5) * mm});
            skLineSegment(sketch, "E151.MirrorCS", {"start": v(145, 67.5) * mm, "end": v(150, 67.5) * mm});
            skLineSegment(sketch, "E152.MirrorCS", {"start": v(145, -17.5) * mm, "end": v(150, -17.5) * mm});
            skLineSegment(sketch, "E153.MirrorCS", {"start": v(145, -67.5) * mm, "end": v(150, -67.5) * mm});
            skLineSegment(sketch, "E154.MirrorCS", {"start": v(145, -57.5) * mm, "end": v(150, -57.5) * mm});
            skLineSegment(sketch, "E155.MirrorCS", {"start": v(145, 57.5) * mm, "end": v(150, 57.5) * mm});
            skLineSegment(sketch, "E156.MirrorCS", {"start": v(145, 42.5) * mm, "end": v(150, 42.5) * mm});
            skLineSegment(sketch, "E157.MirrorCS", {"start": v(145, 7.5) * mm, "end": v(150, 7.5) * mm});
            skLineSegment(sketch, "E158.MirrorCS", {"start": v(145, -7.5) * mm, "end": v(150, -7.5) * mm});
            skLineSegment(sketch, "E159.MirrorCS", {"start": v(145, 82.5) * mm, "end": v(150, 82.5) * mm});
            skLineSegment(sketch, "E160.MirrorCS", {"start": v(145, -82.5) * mm, "end": v(150, -82.5) * mm});
            skLineSegment(sketch, "E161.MirrorCS", {"start": v(150, 57.5) * mm, "end": v(150, 67.5) * mm});
            skLineSegment(sketch, "E162.MirrorCS", {"start": v(150, -42.5) * mm, "end": v(150, -32.5) * mm});
            skLineSegment(sketch, "E163.MirrorCS", {"start": v(150, -67.5) * mm, "end": v(150, -57.5) * mm});
            skLineSegment(sketch, "E164.MirrorCS", {"start": v(145, 67.5) * mm, "end": v(145, 82.5) * mm});
            skLineSegment(sketch, "E165.MirrorCS", {"start": v(145, -42.5) * mm, "end": v(145, -57.5) * mm});
            skLineSegment(sketch, "E166.MirrorCS", {"start": v(145, 7.5) * mm, "end": v(145, -7.5) * mm});
            skLineSegment(sketch, "E167.MirrorCS", {"start": v(145, -67.5) * mm, "end": v(145, -82.5) * mm});
            skLineSegment(sketch, "E168.MirrorCS", {"start": v(145, -17.5) * mm, "end": v(145, -32.5) * mm});
            skLineSegment(sketch, "E169.MirrorCS", {"start": v(150, 7.5) * mm, "end": v(150, 17.5) * mm});
            skLineSegment(sketch, "E170.MirrorCS", {"start": v(150, -17.5) * mm, "end": v(150, -7.5) * mm});
            skLineSegment(sketch, "E171.MirrorCS", {"start": v(145, 17.5) * mm, "end": v(145, 32.5) * mm});
            skLineSegment(sketch, "E172.MirrorCS", {"start": v(145, 42.5) * mm, "end": v(145, 57.5) * mm});
            skLineSegment(sketch, "E173.MirrorCS", {"start": v(150, 32.5) * mm, "end": v(150, 42.5) * mm});
            skLineSegment(sketch, "E174.MirrorCS", {"start": v(150, 82.5) * mm, "end": v(150, -82.5) * mm});
            skSolve(sketch);
        }
        {
            var Q0;
            Q0 = qSketchRegion(id + "F2", true);
            var Q1;
            Q1=makeQuery(id+"F1.opExtrude","CAP_FACE",FACE,{"disambiguationData":[OSD([sQuery(id+"F0.wireOp",EDGE,"E0.bottom"),sQuery(id+"F0.wireOp",EDGE,"E0.top"),sQuery(id+"F0.wireOp",EDGE,"E0.left"),sQuery(id+"F0.wireOp",EDGE,"E0.right"),sQuery(id+"F0.wireOp",EDGE,"E7.1.0.0"),sQuery(id+"F0.wireOp",EDGE,"E7.1.0.1"),sQuery(id+"F0.wireOp",EDGE,"E7.1.0.2"),sQuery(id+"F0.wireOp",EDGE,"E7.2.0.0"),sQuery(id+"F0.wireOp",EDGE,"E7.2.0.1"),sQuery(id+"F0.wireOp",EDGE,"E7.2.0.2"),sQuery(id+"F0.wireOp",EDGE,"E7.3.0.0"),sQuery(id+"F0.wireOp",EDGE,"E7.3.0.1"),sQuery(id+"F0.wireOp",EDGE,"E7.3.0.2"),sQuery(id+"F0.wireOp",EDGE,"E7.4.0.0"),sQuery(id+"F0.wireOp",EDGE,"E7.4.0.1"),sQuery(id+"F0.wireOp",EDGE,"E7.4.0.2"),sQuery(id+"F0.wireOp",EDGE,"E8.MirrorCS"),sQuery(id+"F0.wireOp",EDGE,"E9.MirrorCS"),sQuery(id+"F0.wireOp",EDGE,"E10.MirrorCS"),sQuery(id+"F0.wireOp",EDGE,"E4"),sQuery(id+"F0.wireOp",EDGE,"E2"),sQuery(id+"F0.wireOp",EDGE,"E11.MirrorCS"),sQuery(id+"F0.wireOp",EDGE,"E12.MirrorCS"),sQuery(id+"F0.wireOp",EDGE,"E13.MirrorCS"),sQuery(id+"F0.wireOp",EDGE,"E14.MirrorCS"),sQuery(id+"F0.wireOp",EDGE,"E15.MirrorCS"),sQuery(id+"F0.wireOp",EDGE,"E16.MirrorCS"),sQuery(id+"F0.wireOp",EDGE,"E17.MirrorCS"),sQuery(id+"F0.wireOp",EDGE,"E18.MirrorCS"),sQuery(id+"F0.wireOp",EDGE,"E20.MirrorCS"),sQuery(id+"F0.wireOp",EDGE,"E21.MirrorCS"),sQuery(id+"F0.wireOp",EDGE,"E25.MirrorCS"),sQuery(id+"F0.wireOp",EDGE,"E22.MirrorCS"),sQuery(id+"F0.wireOp",EDGE,"E26.MirrorCS"),sQuery(id+"F0.wireOp",EDGE,"E27.MirrorCS"),sQuery(id+"F0.wireOp",EDGE,"E28.MirrorCS"),sQuery(id+"F0.wireOp",EDGE,"E29.MirrorCS"),sQuery(id+"F0.wireOp",EDGE,"E30.MirrorCS"),sQuery(id+"F0.wireOp",EDGE,"E31.MirrorCS"),sQuery(id+"F0.wireOp",EDGE,"E32.MirrorCS"),sQuery(id+"F0.wireOp",EDGE,"E33.MirrorCS"),sQuery(id+"F0.wireOp",EDGE,"E34.MirrorCS"),sQuery(id+"F0.wireOp",EDGE,"E35.MirrorCS"),sQuery(id+"F0.wireOp",EDGE,"E37.MirrorCS"),sQuery(id+"F0.wireOp",EDGE,"E38.MirrorCS"),sQuery(id+"F0.wireOp",EDGE,"E39.MirrorCS"),sQuery(id+"F0.wireOp",EDGE,"E40.MirrorCS"),sQuery(id+"F0.wireOp",EDGE,"E41.MirrorCS"),sQuery(id+"F0.wireOp",EDGE,"E42.MirrorCS"),sQuery(id+"F0.wireOp",EDGE,"E43.MirrorCS"),sQuery(id+"F0.wireOp",EDGE,"E44.MirrorCS"),sQuery(id+"F0.wireOp",EDGE,"E45.MirrorCS"),sQuery(id+"F0.wireOp",EDGE,"E46.MirrorCS"),sQuery(id+"F0.wireOp",EDGE,"E47.MirrorCS"),sQuery(id+"F0.wireOp",EDGE,"E48.MirrorCS"),sQuery(id+"F0.wireOp",EDGE,"E49.MirrorCS"),sQuery(id+"F0.wireOp",EDGE,"E50.MirrorCS"),sQuery(id+"F0.wireOp",EDGE,"E51.MirrorCS"),sQuery(id+"F0.wireOp",EDGE,"E54.MirrorCS"),sQuery(id+"F0.wireOp",EDGE,"E59.0.1.0"),sQuery(id+"F0.wireOp",EDGE,"E59.0.1.1"),sQuery(id+"F0.wireOp",EDGE,"E59.0.1.2"),sQuery(id+"F0.wireOp",EDGE,"E59.0.2.0"),sQuery(id+"F0.wireOp",EDGE,"E59.0.2.1"),sQuery(id+"F0.wireOp",EDGE,"E59.0.2.2"),sQuery(id+"F0.wireOp",EDGE,"E59.0.3.0"),sQuery(id+"F0.wireOp",EDGE,"E59.0.3.1"),sQuery(id+"F0.wireOp",EDGE,"E59.0.3.2"),sQuery(id+"F0.wireOp",EDGE,"E60.MirrorCS"),sQuery(id+"F0.wireOp",EDGE,"E56"),sQuery(id+"F0.wireOp",EDGE,"E61.MirrorCS"),sQuery(id+"F0.wireOp",EDGE,"E62.MirrorCS"),sQuery(id+"F0.wireOp",EDGE,"E57"),sQuery(id+"F0.wireOp",EDGE,"E63.MirrorCS"),sQuery(id+"F0.wireOp",EDGE,"E64.MirrorCS"),sQuery(id+"F0.wireOp",EDGE,"E65.MirrorCS"),sQuery(id+"F0.wireOp",EDGE,"E66.MirrorCS"),sQuery(id+"F0.wireOp",EDGE,"E67.MirrorCS"),sQuery(id+"F0.wireOp",EDGE,"E68.MirrorCS"),sQuery(id+"F0.wireOp",EDGE,"E70.MirrorCS"),sQuery(id+"F0.wireOp",EDGE,"E71.MirrorCS"),sQuery(id+"F0.wireOp",EDGE,"E72.MirrorCS"),sQuery(id+"F0.wireOp",EDGE,"E75.MirrorCS"),sQuery(id+"F0.wireOp",EDGE,"E76.MirrorCS"),sQuery(id+"F0.wireOp",EDGE,"E77.MirrorCS"),sQuery(id+"F0.wireOp",EDGE,"E78.MirrorCS"),sQuery(id+"F0.wireOp",EDGE,"E79.MirrorCS"),sQuery(id+"F0.wireOp",EDGE,"E80.MirrorCS"),sQuery(id+"F0.wireOp",EDGE,"E81.MirrorCS"),sQuery(id+"F0.wireOp",EDGE,"E82.MirrorCS"),sQuery(id+"F0.wireOp",EDGE,"E84.MirrorCS"),sQuery(id+"F0.wireOp",EDGE,"E85.MirrorCS"),sQuery(id+"F0.wireOp",EDGE,"E86.MirrorCS"),sQuery(id+"F0.wireOp",EDGE,"E87.MirrorCS"),sQuery(id+"F0.wireOp",EDGE,"E88.MirrorCS"),sQuery(id+"F0.wireOp",EDGE,"E89.MirrorCS"),sQuery(id+"F0.wireOp",EDGE,"E90.MirrorCS"),sQuery(id+"F0.wireOp",EDGE,"E91.MirrorCS"),sQuery(id+"F0.wireOp",EDGE,"E92.MirrorCS"),sQuery(id+"F0.wireOp",EDGE,"E94.MirrorCS"),sQuery(id+"F0.wireOp",EDGE,"E96.MirrorCS")])],"isStart":true});
            extrude(context, id + "F3", {"entities" : qUnion([Q0]), "endBound" : BoundingType.UP_TO_SURFACE, "oppositeDirection" : true, "endBoundEntityFace" : qUnion([Q1]), "depth" : 25 * mm});
        }
        {
            var Q0;
            Q0=makeQuery(id+"F1.opExtrude","CAP_FACE",FACE,{"disambiguationData":[OSD([sQuery(id+"F0.wireOp",EDGE,"E0.bottom"),sQuery(id+"F0.wireOp",EDGE,"E0.top"),sQuery(id+"F0.wireOp",EDGE,"E0.left"),sQuery(id+"F0.wireOp",EDGE,"E0.right"),sQuery(id+"F0.wireOp",EDGE,"E7.1.0.0"),sQuery(id+"F0.wireOp",EDGE,"E7.1.0.1"),sQuery(id+"F0.wireOp",EDGE,"E7.1.0.2"),sQuery(id+"F0.wireOp",EDGE,"E7.2.0.0"),sQuery(id+"F0.wireOp",EDGE,"E7.2.0.1"),sQuery(id+"F0.wireOp",EDGE,"E7.2.0.2"),sQuery(id+"F0.wireOp",EDGE,"E7.3.0.0"),sQuery(id+"F0.wireOp",EDGE,"E7.3.0.1"),sQuery(id+"F0.wireOp",EDGE,"E7.3.0.2"),sQuery(id+"F0.wireOp",EDGE,"E7.4.0.0"),sQuery(id+"F0.wireOp",EDGE,"E7.4.0.1"),sQuery(id+"F0.wireOp",EDGE,"E7.4.0.2"),sQuery(id+"F0.wireOp",EDGE,"E8.MirrorCS"),sQuery(id+"F0.wireOp",EDGE,"E9.MirrorCS"),sQuery(id+"F0.wireOp",EDGE,"E10.MirrorCS"),sQuery(id+"F0.wireOp",EDGE,"E4"),sQuery(id+"F0.wireOp",EDGE,"E2"),sQuery(id+"F0.wireOp",EDGE,"E11.MirrorCS"),sQuery(id+"F0.wireOp",EDGE,"E12.MirrorCS"),sQuery(id+"F0.wireOp",EDGE,"E13.MirrorCS"),sQuery(id+"F0.wireOp",EDGE,"E14.MirrorCS"),sQuery(id+"F0.wireOp",EDGE,"E15.MirrorCS"),sQuery(id+"F0.wireOp",EDGE,"E16.MirrorCS"),sQuery(id+"F0.wireOp",EDGE,"E17.MirrorCS"),sQuery(id+"F0.wireOp",EDGE,"E18.MirrorCS"),sQuery(id+"F0.wireOp",EDGE,"E20.MirrorCS"),sQuery(id+"F0.wireOp",EDGE,"E21.MirrorCS"),sQuery(id+"F0.wireOp",EDGE,"E25.MirrorCS"),sQuery(id+"F0.wireOp",EDGE,"E22.MirrorCS"),sQuery(id+"F0.wireOp",EDGE,"E26.MirrorCS"),sQuery(id+"F0.wireOp",EDGE,"E27.MirrorCS"),sQuery(id+"F0.wireOp",EDGE,"E28.MirrorCS"),sQuery(id+"F0.wireOp",EDGE,"E29.MirrorCS"),sQuery(id+"F0.wireOp",EDGE,"E30.MirrorCS"),sQuery(id+"F0.wireOp",EDGE,"E31.MirrorCS"),sQuery(id+"F0.wireOp",EDGE,"E32.MirrorCS"),sQuery(id+"F0.wireOp",EDGE,"E33.MirrorCS"),sQuery(id+"F0.wireOp",EDGE,"E34.MirrorCS"),sQuery(id+"F0.wireOp",EDGE,"E35.MirrorCS"),sQuery(id+"F0.wireOp",EDGE,"E37.MirrorCS"),sQuery(id+"F0.wireOp",EDGE,"E38.MirrorCS"),sQuery(id+"F0.wireOp",EDGE,"E39.MirrorCS"),sQuery(id+"F0.wireOp",EDGE,"E40.MirrorCS"),sQuery(id+"F0.wireOp",EDGE,"E41.MirrorCS"),sQuery(id+"F0.wireOp",EDGE,"E42.MirrorCS"),sQuery(id+"F0.wireOp",EDGE,"E43.MirrorCS"),sQuery(id+"F0.wireOp",EDGE,"E44.MirrorCS"),sQuery(id+"F0.wireOp",EDGE,"E45.MirrorCS"),sQuery(id+"F0.wireOp",EDGE,"E46.MirrorCS"),sQuery(id+"F0.wireOp",EDGE,"E47.MirrorCS"),sQuery(id+"F0.wireOp",EDGE,"E48.MirrorCS"),sQuery(id+"F0.wireOp",EDGE,"E49.MirrorCS"),sQuery(id+"F0.wireOp",EDGE,"E50.MirrorCS"),sQuery(id+"F0.wireOp",EDGE,"E51.MirrorCS"),sQuery(id+"F0.wireOp",EDGE,"E54.MirrorCS"),sQuery(id+"F0.wireOp",EDGE,"E59.0.1.0"),sQuery(id+"F0.wireOp",EDGE,"E59.0.1.1"),sQuery(id+"F0.wireOp",EDGE,"E59.0.1.2"),sQuery(id+"F0.wireOp",EDGE,"E59.0.2.0"),sQuery(id+"F0.wireOp",EDGE,"E59.0.2.1"),sQuery(id+"F0.wireOp",EDGE,"E59.0.2.2"),sQuery(id+"F0.wireOp",EDGE,"E59.0.3.0"),sQuery(id+"F0.wireOp",EDGE,"E59.0.3.1"),sQuery(id+"F0.wireOp",EDGE,"E59.0.3.2"),sQuery(id+"F0.wireOp",EDGE,"E60.MirrorCS"),sQuery(id+"F0.wireOp",EDGE,"E56"),sQuery(id+"F0.wireOp",EDGE,"E61.MirrorCS"),sQuery(id+"F0.wireOp",EDGE,"E62.MirrorCS"),sQuery(id+"F0.wireOp",EDGE,"E57"),sQuery(id+"F0.wireOp",EDGE,"E63.MirrorCS"),sQuery(id+"F0.wireOp",EDGE,"E64.MirrorCS"),sQuery(id+"F0.wireOp",EDGE,"E65.MirrorCS"),sQuery(id+"F0.wireOp",EDGE,"E66.MirrorCS"),sQuery(id+"F0.wireOp",EDGE,"E67.MirrorCS"),sQuery(id+"F0.wireOp",EDGE,"E68.MirrorCS"),sQuery(id+"F0.wireOp",EDGE,"E70.MirrorCS"),sQuery(id+"F0.wireOp",EDGE,"E71.MirrorCS"),sQuery(id+"F0.wireOp",EDGE,"E72.MirrorCS"),sQuery(id+"F0.wireOp",EDGE,"E75.MirrorCS"),sQuery(id+"F0.wireOp",EDGE,"E76.MirrorCS"),sQuery(id+"F0.wireOp",EDGE,"E77.MirrorCS"),sQuery(id+"F0.wireOp",EDGE,"E78.MirrorCS"),sQuery(id+"F0.wireOp",EDGE,"E79.MirrorCS"),sQuery(id+"F0.wireOp",EDGE,"E80.MirrorCS"),sQuery(id+"F0.wireOp",EDGE,"E81.MirrorCS"),sQuery(id+"F0.wireOp",EDGE,"E82.MirrorCS"),sQuery(id+"F0.wireOp",EDGE,"E84.MirrorCS"),sQuery(id+"F0.wireOp",EDGE,"E85.MirrorCS"),sQuery(id+"F0.wireOp",EDGE,"E86.MirrorCS"),sQuery(id+"F0.wireOp",EDGE,"E87.MirrorCS"),sQuery(id+"F0.wireOp",EDGE,"E88.MirrorCS"),sQuery(id+"F0.wireOp",EDGE,"E89.MirrorCS"),sQuery(id+"F0.wireOp",EDGE,"E90.MirrorCS"),sQuery(id+"F0.wireOp",EDGE,"E91.MirrorCS"),sQuery(id+"F0.wireOp",EDGE,"E92.MirrorCS"),sQuery(id+"F0.wireOp",EDGE,"E94.MirrorCS"),sQuery(id+"F0.wireOp",EDGE,"E96.MirrorCS")])],"isStart":false});
            var sketch = newSketch(context, id + "F4", { "sketchPlane" : qUnion([Q0])});
            skPoint(sketch, "E175.0", {"position": v(127.5, 96) * mm});
            skLineSegment(sketch, "E176.bottom", {"start": v(-150, 100) * mm, "end": v(150, 100) * mm});
            skLineSegment(sketch, "E176.top", {"start": v(-150, 96) * mm, "end": v(150, 96) * mm});
            skLineSegment(sketch, "E176.left", {"start": v(-150, 100) * mm, "end": v(-150, 96) * mm});
            skLineSegment(sketch, "E176.right", {"start": v(150, 100) * mm, "end": v(150, 96) * mm});
            skSolve(sketch);
        }
        {
            var Q0;
            Q0 = qSketchRegion(id + "F4", true);
            extrude(context, id + "F5", {"entities" : qUnion([Q0]), "depth" : 96 * mm});
        }
        {
            var Q0;
            Q0=makeQuery(id+"F3.opExtrude","SWEPT_BODY",BODY,{"disambiguationData":[OSD([sQuery(id+"F2.wireOp",EDGE,"E97.59"),sQuery(id+"F2.wireOp",EDGE,"E97.60"),sQuery(id+"F2.wireOp",EDGE,"E97.75"),sQuery(id+"F2.wireOp",EDGE,"E98")])]});
            var Q1;
            Q1=makeQuery(id+"F3.opExtrude","SWEPT_BODY",BODY,{"disambiguationData":[OSD([sQuery(id+"F2.wireOp",EDGE,"E97.47"),sQuery(id+"F2.wireOp",EDGE,"E97.61"),sQuery(id+"F2.wireOp",EDGE,"E97.98"),sQuery(id+"F2.wireOp",EDGE,"E102.trimOffspring")])]});
            var Q2;
            Q2=makeQuery(id+"F3.opExtrude","SWEPT_BODY",BODY,{"disambiguationData":[OSD([sQuery(id+"F2.wireOp",EDGE,"E97.43"),sQuery(id+"F2.wireOp",EDGE,"E97.74"),sQuery(id+"F2.wireOp",EDGE,"E97.87"),sQuery(id+"F2.wireOp",EDGE,"E101.trimOffspring")])]});
            var Q3;
            Q3=makeQuery(id+"F3.opExtrude","SWEPT_BODY",BODY,{"disambiguationData":[OSD([sQuery(id+"F2.wireOp",EDGE,"E97.81"),sQuery(id+"F2.wireOp",EDGE,"E97.90"),sQuery(id+"F2.wireOp",EDGE,"E97.104"),sQuery(id+"F2.wireOp",EDGE,"E100.trimOffspring")])]});
            var Q4;
            Q4=makeQuery(id+"F3.opExtrude","SWEPT_BODY",BODY,{"disambiguationData":[OSD([sQuery(id+"F2.wireOp",EDGE,"E97.56"),sQuery(id+"F2.wireOp",EDGE,"E97.80"),sQuery(id+"F2.wireOp",EDGE,"E97.100"),sQuery(id+"F2.wireOp",EDGE,"E99.trimOffspring")])]});
            var Q5;
            Q5=makeQuery(id+"F3.opExtrude","SWEPT_BODY",BODY,{"disambiguationData":[OSD([sQuery(id+"F2.wireOp",EDGE,"E97.72"),sQuery(id+"F2.wireOp",EDGE,"E97.78"),sQuery(id+"F2.wireOp",EDGE,"E97.85"),sQuery(id+"F2.wireOp",EDGE,"E103.trimOffspring")])]});
            var Q6;
            Q6=makeQuery(id+"F3.opExtrude","SWEPT_BODY",BODY,{"disambiguationData":[OSD([sQuery(id+"F2.wireOp",EDGE,"E97.42"),sQuery(id+"F2.wireOp",EDGE,"E97.50"),sQuery(id+"F2.wireOp",EDGE,"E97.91"),sQuery(id+"F2.wireOp",EDGE,"E103.trimOffspring")])]});
            var Q7;
            Q7=makeQuery(id+"F3.opExtrude","SWEPT_BODY",BODY,{"disambiguationData":[OSD([sQuery(id+"F2.wireOp",EDGE,"E97.48"),sQuery(id+"F2.wireOp",EDGE,"E97.57"),sQuery(id+"F2.wireOp",EDGE,"E97.64"),sQuery(id+"F2.wireOp",EDGE,"E103.trimOffspring")])]});
            var Q8;
            Q8=makeQuery(id+"F3.opExtrude","SWEPT_BODY",BODY,{"disambiguationData":[OSD([sQuery(id+"F2.wireOp",EDGE,"E97.79"),sQuery(id+"F2.wireOp",EDGE,"E97.86"),sQuery(id+"F2.wireOp",EDGE,"E97.92"),sQuery(id+"F2.wireOp",EDGE,"E103.trimOffspring")])]});
            var Q9;
            Q9=makeQuery(id+"F5.opExtrude","SWEPT_BODY",BODY,{"disambiguationData":[OSD([sQuery(id+"F4.wireOp",EDGE,"E176.bottom"),sQuery(id+"F4.wireOp",EDGE,"E176.top"),sQuery(id+"F4.wireOp",EDGE,"E176.left"),sQuery(id+"F4.wireOp",EDGE,"E176.right")])]});
            booleanBodies(context, id + "F6", {"operationType" : BooleanOperationType.UNION, "tools" : qUnion([Q0, Q1, Q2, Q3, Q4, Q5, Q6, Q7, Q8, Q9])});
        }
        {
            var Q0;
            Q0=makeQuery(id+"F3.opExtrude","SWEPT_BODY",BODY,{"disambiguationData":[OSD([sQuery(id+"F2.wireOp",EDGE,"E97.59"),sQuery(id+"F2.wireOp",EDGE,"E97.60"),sQuery(id+"F2.wireOp",EDGE,"E97.75"),sQuery(id+"F2.wireOp",EDGE,"E98")])]});
            var Q1;
            Q1=qCreatedBy(makeId("Front.planeOp"),FACE);
            mirror(context, id + "F7", {"entities" : qUnion([Q0]), "mirrorPlane" : qUnion([Q1])});
        }
        {
            var Q0;
            Q0=makeQuery(id+"F3.opExtrude","SWEPT_BODY",BODY,{"disambiguationData":[OSD([sQuery(id+"F2.wireOp",EDGE,"E105.MirrorCS"),sQuery(id+"F2.wireOp",EDGE,"E117.MirrorCS"),sQuery(id+"F2.wireOp",EDGE,"E135.MirrorCS"),sQuery(id+"F2.wireOp",EDGE,"E122.MirrorCS")])]});
            var Q1;
            Q1=makeQuery(id+"F7.opPattern","COPY",BODY,{"derivedFrom":makeQuery(id+"F3.opExtrude","SWEPT_BODY",BODY,{"disambiguationData":[OSD([sQuery(id+"F2.wireOp",EDGE,"E97.59"),sQuery(id+"F2.wireOp",EDGE,"E97.60"),sQuery(id+"F2.wireOp",EDGE,"E97.75"),sQuery(id+"F2.wireOp",EDGE,"E98")])]}),"instanceName":"1"});
            var Q2;
            Q2=makeQuery(id+"F3.opExtrude","SWEPT_BODY",BODY,{"disambiguationData":[OSD([sQuery(id+"F2.wireOp",EDGE,"E113.MirrorCS"),sQuery(id+"F2.wireOp",EDGE,"E104.MirrorCS"),sQuery(id+"F2.wireOp",EDGE,"E125.MirrorCS"),sQuery(id+"F2.wireOp",EDGE,"E144.MirrorCS")])]});
            var Q3;
            Q3=makeQuery(id+"F3.opExtrude","SWEPT_BODY",BODY,{"disambiguationData":[OSD([sQuery(id+"F2.wireOp",EDGE,"E110.MirrorCS"),sQuery(id+"F2.wireOp",EDGE,"E108.MirrorCS"),sQuery(id+"F2.wireOp",EDGE,"E137.MirrorCS"),sQuery(id+"F2.wireOp",EDGE,"E128.MirrorCS")])]});
            var Q4;
            Q4=makeQuery(id+"F3.opExtrude","SWEPT_BODY",BODY,{"disambiguationData":[OSD([sQuery(id+"F2.wireOp",EDGE,"E111.MirrorCS"),sQuery(id+"F2.wireOp",EDGE,"E112.MirrorCS"),sQuery(id+"F2.wireOp",EDGE,"E142.MirrorCS"),sQuery(id+"F2.wireOp",EDGE,"E129.MirrorCS")])]});
            var Q5;
            Q5=makeQuery(id+"F3.opExtrude","SWEPT_BODY",BODY,{"disambiguationData":[OSD([sQuery(id+"F2.wireOp",EDGE,"E109.MirrorCS"),sQuery(id+"F2.wireOp",EDGE,"E106.MirrorCS"),sQuery(id+"F2.wireOp",EDGE,"E134.MirrorCS"),sQuery(id+"F2.wireOp",EDGE,"E126.MirrorCS")])]});
            var Q6;
            Q6=makeQuery(id+"F3.opExtrude","SWEPT_BODY",BODY,{"disambiguationData":[OSD([sQuery(id+"F2.wireOp",EDGE,"E107.MirrorCS"),sQuery(id+"F2.wireOp",EDGE,"E114.MirrorCS"),sQuery(id+"F2.wireOp",EDGE,"E123.MirrorCS"),sQuery(id+"F2.wireOp",EDGE,"E140.MirrorCS")])]});
            var Q7;
            Q7=makeQuery(id+"F3.opExtrude","SWEPT_BODY",BODY,{"disambiguationData":[OSD([sQuery(id+"F2.wireOp",EDGE,"E115.MirrorCS"),sQuery(id+"F2.wireOp",EDGE,"E121.MirrorCS"),sQuery(id+"F2.wireOp",EDGE,"E140.MirrorCS"),sQuery(id+"F2.wireOp",EDGE,"E133.MirrorCS")])]});
            var Q8;
            Q8=makeQuery(id+"F3.opExtrude","SWEPT_BODY",BODY,{"disambiguationData":[OSD([sQuery(id+"F2.wireOp",EDGE,"E116.MirrorCS"),sQuery(id+"F2.wireOp",EDGE,"E118.MirrorCS"),sQuery(id+"F2.wireOp",EDGE,"E140.MirrorCS"),sQuery(id+"F2.wireOp",EDGE,"E124.MirrorCS")])]});
            var Q9;
            Q9=makeQuery(id+"F3.opExtrude","SWEPT_BODY",BODY,{"disambiguationData":[OSD([sQuery(id+"F2.wireOp",EDGE,"E120.MirrorCS"),sQuery(id+"F2.wireOp",EDGE,"E119.MirrorCS"),sQuery(id+"F2.wireOp",EDGE,"E140.MirrorCS"),sQuery(id+"F2.wireOp",EDGE,"E127.MirrorCS")])]});
            booleanBodies(context, id + "F8", {"operationType" : BooleanOperationType.UNION, "tools" : qUnion([Q0, Q1, Q2, Q3, Q4, Q5, Q6, Q7, Q8, Q9])});
        }
        {
            var Q0;
            Q0=makeQuery(id+"F1.opExtrude","CAP_FACE",FACE,{"disambiguationData":[OSD([sQuery(id+"F0.wireOp",EDGE,"E0.bottom"),sQuery(id+"F0.wireOp",EDGE,"E0.top"),sQuery(id+"F0.wireOp",EDGE,"E0.left"),sQuery(id+"F0.wireOp",EDGE,"E0.right"),sQuery(id+"F0.wireOp",EDGE,"E7.1.0.0"),sQuery(id+"F0.wireOp",EDGE,"E7.1.0.1"),sQuery(id+"F0.wireOp",EDGE,"E7.1.0.2"),sQuery(id+"F0.wireOp",EDGE,"E7.2.0.0"),sQuery(id+"F0.wireOp",EDGE,"E7.2.0.1"),sQuery(id+"F0.wireOp",EDGE,"E7.2.0.2"),sQuery(id+"F0.wireOp",EDGE,"E7.3.0.0"),sQuery(id+"F0.wireOp",EDGE,"E7.3.0.1"),sQuery(id+"F0.wireOp",EDGE,"E7.3.0.2"),sQuery(id+"F0.wireOp",EDGE,"E7.4.0.0"),sQuery(id+"F0.wireOp",EDGE,"E7.4.0.1"),sQuery(id+"F0.wireOp",EDGE,"E7.4.0.2"),sQuery(id+"F0.wireOp",EDGE,"E8.MirrorCS"),sQuery(id+"F0.wireOp",EDGE,"E9.MirrorCS"),sQuery(id+"F0.wireOp",EDGE,"E10.MirrorCS"),sQuery(id+"F0.wireOp",EDGE,"E4"),sQuery(id+"F0.wireOp",EDGE,"E2"),sQuery(id+"F0.wireOp",EDGE,"E11.MirrorCS"),sQuery(id+"F0.wireOp",EDGE,"E12.MirrorCS"),sQuery(id+"F0.wireOp",EDGE,"E13.MirrorCS"),sQuery(id+"F0.wireOp",EDGE,"E14.MirrorCS"),sQuery(id+"F0.wireOp",EDGE,"E15.MirrorCS"),sQuery(id+"F0.wireOp",EDGE,"E16.MirrorCS"),sQuery(id+"F0.wireOp",EDGE,"E17.MirrorCS"),sQuery(id+"F0.wireOp",EDGE,"E18.MirrorCS"),sQuery(id+"F0.wireOp",EDGE,"E20.MirrorCS"),sQuery(id+"F0.wireOp",EDGE,"E21.MirrorCS"),sQuery(id+"F0.wireOp",EDGE,"E25.MirrorCS"),sQuery(id+"F0.wireOp",EDGE,"E22.MirrorCS"),sQuery(id+"F0.wireOp",EDGE,"E26.MirrorCS"),sQuery(id+"F0.wireOp",EDGE,"E27.MirrorCS"),sQuery(id+"F0.wireOp",EDGE,"E28.MirrorCS"),sQuery(id+"F0.wireOp",EDGE,"E29.MirrorCS"),sQuery(id+"F0.wireOp",EDGE,"E30.MirrorCS"),sQuery(id+"F0.wireOp",EDGE,"E31.MirrorCS"),sQuery(id+"F0.wireOp",EDGE,"E32.MirrorCS"),sQuery(id+"F0.wireOp",EDGE,"E33.MirrorCS"),sQuery(id+"F0.wireOp",EDGE,"E34.MirrorCS"),sQuery(id+"F0.wireOp",EDGE,"E35.MirrorCS"),sQuery(id+"F0.wireOp",EDGE,"E37.MirrorCS"),sQuery(id+"F0.wireOp",EDGE,"E38.MirrorCS"),sQuery(id+"F0.wireOp",EDGE,"E39.MirrorCS"),sQuery(id+"F0.wireOp",EDGE,"E40.MirrorCS"),sQuery(id+"F0.wireOp",EDGE,"E41.MirrorCS"),sQuery(id+"F0.wireOp",EDGE,"E42.MirrorCS"),sQuery(id+"F0.wireOp",EDGE,"E43.MirrorCS"),sQuery(id+"F0.wireOp",EDGE,"E44.MirrorCS"),sQuery(id+"F0.wireOp",EDGE,"E45.MirrorCS"),sQuery(id+"F0.wireOp",EDGE,"E46.MirrorCS"),sQuery(id+"F0.wireOp",EDGE,"E47.MirrorCS"),sQuery(id+"F0.wireOp",EDGE,"E48.MirrorCS"),sQuery(id+"F0.wireOp",EDGE,"E49.MirrorCS"),sQuery(id+"F0.wireOp",EDGE,"E50.MirrorCS"),sQuery(id+"F0.wireOp",EDGE,"E51.MirrorCS"),sQuery(id+"F0.wireOp",EDGE,"E54.MirrorCS"),sQuery(id+"F0.wireOp",EDGE,"E59.0.1.0"),sQuery(id+"F0.wireOp",EDGE,"E59.0.1.1"),sQuery(id+"F0.wireOp",EDGE,"E59.0.1.2"),sQuery(id+"F0.wireOp",EDGE,"E59.0.2.0"),sQuery(id+"F0.wireOp",EDGE,"E59.0.2.1"),sQuery(id+"F0.wireOp",EDGE,"E59.0.2.2"),sQuery(id+"F0.wireOp",EDGE,"E59.0.3.0"),sQuery(id+"F0.wireOp",EDGE,"E59.0.3.1"),sQuery(id+"F0.wireOp",EDGE,"E59.0.3.2"),sQuery(id+"F0.wireOp",EDGE,"E60.MirrorCS"),sQuery(id+"F0.wireOp",EDGE,"E56"),sQuery(id+"F0.wireOp",EDGE,"E61.MirrorCS"),sQuery(id+"F0.wireOp",EDGE,"E62.MirrorCS"),sQuery(id+"F0.wireOp",EDGE,"E57"),sQuery(id+"F0.wireOp",EDGE,"E63.MirrorCS"),sQuery(id+"F0.wireOp",EDGE,"E64.MirrorCS"),sQuery(id+"F0.wireOp",EDGE,"E65.MirrorCS"),sQuery(id+"F0.wireOp",EDGE,"E66.MirrorCS"),sQuery(id+"F0.wireOp",EDGE,"E67.MirrorCS"),sQuery(id+"F0.wireOp",EDGE,"E68.MirrorCS"),sQuery(id+"F0.wireOp",EDGE,"E70.MirrorCS"),sQuery(id+"F0.wireOp",EDGE,"E71.MirrorCS"),sQuery(id+"F0.wireOp",EDGE,"E72.MirrorCS"),sQuery(id+"F0.wireOp",EDGE,"E75.MirrorCS"),sQuery(id+"F0.wireOp",EDGE,"E76.MirrorCS"),sQuery(id+"F0.wireOp",EDGE,"E77.MirrorCS"),sQuery(id+"F0.wireOp",EDGE,"E78.MirrorCS"),sQuery(id+"F0.wireOp",EDGE,"E79.MirrorCS"),sQuery(id+"F0.wireOp",EDGE,"E80.MirrorCS"),sQuery(id+"F0.wireOp",EDGE,"E81.MirrorCS"),sQuery(id+"F0.wireOp",EDGE,"E82.MirrorCS"),sQuery(id+"F0.wireOp",EDGE,"E84.MirrorCS"),sQuery(id+"F0.wireOp",EDGE,"E85.MirrorCS"),sQuery(id+"F0.wireOp",EDGE,"E86.MirrorCS"),sQuery(id+"F0.wireOp",EDGE,"E87.MirrorCS"),sQuery(id+"F0.wireOp",EDGE,"E88.MirrorCS"),sQuery(id+"F0.wireOp",EDGE,"E89.MirrorCS"),sQuery(id+"F0.wireOp",EDGE,"E90.MirrorCS"),sQuery(id+"F0.wireOp",EDGE,"E91.MirrorCS"),sQuery(id+"F0.wireOp",EDGE,"E92.MirrorCS"),sQuery(id+"F0.wireOp",EDGE,"E94.MirrorCS"),sQuery(id+"F0.wireOp",EDGE,"E96.MirrorCS")])],"isStart":false});
            var sketch = newSketch(context, id + "F9", { "sketchPlane" : qUnion([Q0])});
            skLineSegment(sketch, "E177.0", {"start": v(145, 7.5) * mm, "end": v(150, 7.5) * mm});
            skLineSegment(sketch, "E177.1", {"start": v(145, -42.5) * mm, "end": v(150, -42.5) * mm});
            skLineSegment(sketch, "E177.2", {"start": v(145, -17.5) * mm, "end": v(150, -17.5) * mm});
            skLineSegment(sketch, "E177.3", {"start": v(145, 82.5) * mm, "end": v(150, 82.5) * mm});
            skLineSegment(sketch, "E177.4", {"start": v(145, 57.5) * mm, "end": v(150, 57.5) * mm});
            skLineSegment(sketch, "E177.5", {"start": v(145, 32.5) * mm, "end": v(150, 32.5) * mm});
            skLineSegment(sketch, "E177.6", {"start": v(145, -67.5) * mm, "end": v(150, -67.5) * mm});
            skPoint(sketch, "E178.0", {"position": v(150, -96) * mm});
            skPoint(sketch, "E179.0", {"position": v(150, 96) * mm});
            skLineSegment(sketch, "E180.bottom", {"start": v(150, -96) * mm, "end": v(145, -96) * mm});
            skLineSegment(sketch, "E180.top", {"start": v(150, 96) * mm, "end": v(145, 96) * mm});
            skLineSegment(sketch, "E180.left", {"start": v(150, -96) * mm, "end": v(150, 96) * mm});
            skLineSegment(sketch, "E180.right", {"start": v(145, -96) * mm, "end": v(145, 96) * mm});
            skLineSegment(sketch, "E181.MirrorCS", {"start": v(-150, 96) * mm, "end": v(-145, 96) * mm});
            skLineSegment(sketch, "E182.MirrorCS", {"start": v(-150, -96) * mm, "end": v(-145, -96) * mm});
            skLineSegment(sketch, "E183.MirrorCS", {"start": v(-145, 57.5) * mm, "end": v(-150, 57.5) * mm});
            skLineSegment(sketch, "E184.MirrorCS", {"start": v(-145, -42.5) * mm, "end": v(-150, -42.5) * mm});
            skLineSegment(sketch, "E185.MirrorCS", {"start": v(-145, -17.5) * mm, "end": v(-150, -17.5) * mm});
            skLineSegment(sketch, "E186.MirrorCS", {"start": v(-145, 32.5) * mm, "end": v(-150, 32.5) * mm});
            skLineSegment(sketch, "E187.MirrorCS", {"start": v(-145, 7.5) * mm, "end": v(-150, 7.5) * mm});
            skLineSegment(sketch, "E188.MirrorCS", {"start": v(-145, -67.5) * mm, "end": v(-150, -67.5) * mm});
            skLineSegment(sketch, "E189.MirrorCS", {"start": v(-145, 82.5) * mm, "end": v(-150, 82.5) * mm});
            skLineSegment(sketch, "E190.MirrorCS", {"start": v(-145, -96) * mm, "end": v(-145, 96) * mm});
            skPoint(sketch, "E191.MirrorP", {"position": v(-150, 96) * mm});
            skPoint(sketch, "E192.MirrorP", {"position": v(-150, -96) * mm});
            skLineSegment(sketch, "E193.MirrorCS", {"start": v(-150, -96) * mm, "end": v(-150, 96) * mm});
            skSolve(sketch);
        }
        {
            var Q0;
            Q0 = qSketchRegion(id + "F9", true);
            extrude(context, id + "F10", {"entities" : qUnion([Q0]), "depth" : 96 * mm});
        }
        {
            var Q0;
            Q0=makeQuery(id+"F3.opExtrude","SWEPT_BODY",BODY,{"disambiguationData":[OSD([sQuery(id+"F2.wireOp",EDGE,"E153.MirrorCS"),sQuery(id+"F2.wireOp",EDGE,"E160.MirrorCS"),sQuery(id+"F2.wireOp",EDGE,"E167.MirrorCS"),sQuery(id+"F2.wireOp",EDGE,"E174.MirrorCS")])]});
            var Q1;
            Q1=makeQuery(id+"F10.opExtrude","SWEPT_BODY",BODY,{"disambiguationData":[OSD([sQuery(id+"F9.wireOp",EDGE,"E180.bottom"),sQuery(id+"F9.wireOp",EDGE,"E180.top"),sQuery(id+"F9.wireOp",EDGE,"E180.left"),sQuery(id+"F9.wireOp",EDGE,"E180.right")])]});
            var Q2;
            Q2=makeQuery(id+"F3.opExtrude","SWEPT_BODY",BODY,{"disambiguationData":[OSD([sQuery(id+"F2.wireOp",EDGE,"E147.MirrorCS"),sQuery(id+"F2.wireOp",EDGE,"E154.MirrorCS"),sQuery(id+"F2.wireOp",EDGE,"E165.MirrorCS"),sQuery(id+"F2.wireOp",EDGE,"E174.MirrorCS")])]});
            var Q3;
            Q3=makeQuery(id+"F3.opExtrude","SWEPT_BODY",BODY,{"disambiguationData":[OSD([sQuery(id+"F2.wireOp",EDGE,"E152.MirrorCS"),sQuery(id+"F2.wireOp",EDGE,"E150.MirrorCS"),sQuery(id+"F2.wireOp",EDGE,"E168.MirrorCS"),sQuery(id+"F2.wireOp",EDGE,"E174.MirrorCS")])]});
            var Q4;
            Q4=makeQuery(id+"F3.opExtrude","SWEPT_BODY",BODY,{"disambiguationData":[OSD([sQuery(id+"F2.wireOp",EDGE,"E157.MirrorCS"),sQuery(id+"F2.wireOp",EDGE,"E158.MirrorCS"),sQuery(id+"F2.wireOp",EDGE,"E166.MirrorCS"),sQuery(id+"F2.wireOp",EDGE,"E174.MirrorCS")])]});
            var Q5;
            Q5=makeQuery(id+"F3.opExtrude","SWEPT_BODY",BODY,{"disambiguationData":[OSD([sQuery(id+"F2.wireOp",EDGE,"E149.MirrorCS"),sQuery(id+"F2.wireOp",EDGE,"E148.MirrorCS"),sQuery(id+"F2.wireOp",EDGE,"E171.MirrorCS"),sQuery(id+"F2.wireOp",EDGE,"E174.MirrorCS")])]});
            var Q6;
            Q6=makeQuery(id+"F3.opExtrude","SWEPT_BODY",BODY,{"disambiguationData":[OSD([sQuery(id+"F2.wireOp",EDGE,"E155.MirrorCS"),sQuery(id+"F2.wireOp",EDGE,"E156.MirrorCS"),sQuery(id+"F2.wireOp",EDGE,"E172.MirrorCS"),sQuery(id+"F2.wireOp",EDGE,"E174.MirrorCS")])]});
            var Q7;
            Q7=makeQuery(id+"F3.opExtrude","SWEPT_BODY",BODY,{"disambiguationData":[OSD([sQuery(id+"F2.wireOp",EDGE,"E151.MirrorCS"),sQuery(id+"F2.wireOp",EDGE,"E159.MirrorCS"),sQuery(id+"F2.wireOp",EDGE,"E164.MirrorCS"),sQuery(id+"F2.wireOp",EDGE,"E174.MirrorCS")])]});
            booleanBodies(context, id + "F11", {"operationType" : BooleanOperationType.UNION, "tools" : qUnion([Q0, Q1, Q2, Q3, Q4, Q5, Q6, Q7])});
        }
        {
            var Q0;
            Q0=makeQuery(id+"F3.opExtrude","SWEPT_BODY",BODY,{"disambiguationData":[OSD([sQuery(id+"F2.wireOp",EDGE,"E145.32"),sQuery(id+"F2.wireOp",EDGE,"E145.33"),sQuery(id+"F2.wireOp",EDGE,"E145.76"),sQuery(id+"F2.wireOp",EDGE,"E146")])]});
            var Q1;
            Q1=makeQuery(id+"F10.opExtrude","SWEPT_BODY",BODY,{"disambiguationData":[OSD([sQuery(id+"F9.wireOp",EDGE,"E181.MirrorCS"),sQuery(id+"F9.wireOp",EDGE,"E182.MirrorCS"),sQuery(id+"F9.wireOp",EDGE,"E190.MirrorCS"),sQuery(id+"F9.wireOp",EDGE,"E193.MirrorCS")])]});
            var Q2;
            Q2=makeQuery(id+"F3.opExtrude","SWEPT_BODY",BODY,{"disambiguationData":[OSD([sQuery(id+"F2.wireOp",EDGE,"E145.54"),sQuery(id+"F2.wireOp",EDGE,"E145.62"),sQuery(id+"F2.wireOp",EDGE,"E145.65"),sQuery(id+"F2.wireOp",EDGE,"E146")])]});
            var Q3;
            Q3=makeQuery(id+"F3.opExtrude","SWEPT_BODY",BODY,{"disambiguationData":[OSD([sQuery(id+"F2.wireOp",EDGE,"E145.35"),sQuery(id+"F2.wireOp",EDGE,"E145.44"),sQuery(id+"F2.wireOp",EDGE,"E145.45"),sQuery(id+"F2.wireOp",EDGE,"E146")])]});
            var Q4;
            Q4=makeQuery(id+"F3.opExtrude","SWEPT_BODY",BODY,{"disambiguationData":[OSD([sQuery(id+"F2.wireOp",EDGE,"E145.47"),sQuery(id+"F2.wireOp",EDGE,"E145.51"),sQuery(id+"F2.wireOp",EDGE,"E145.66"),sQuery(id+"F2.wireOp",EDGE,"E146")])]});
            var Q5;
            Q5=makeQuery(id+"F3.opExtrude","SWEPT_BODY",BODY,{"disambiguationData":[OSD([sQuery(id+"F2.wireOp",EDGE,"E145.34"),sQuery(id+"F2.wireOp",EDGE,"E145.49"),sQuery(id+"F2.wireOp",EDGE,"E145.53"),sQuery(id+"F2.wireOp",EDGE,"E146")])]});
            var Q6;
            Q6=makeQuery(id+"F3.opExtrude","SWEPT_BODY",BODY,{"disambiguationData":[OSD([sQuery(id+"F2.wireOp",EDGE,"E145.75"),sQuery(id+"F2.wireOp",EDGE,"E145.80"),sQuery(id+"F2.wireOp",EDGE,"E145.81"),sQuery(id+"F2.wireOp",EDGE,"E146")])]});
            var Q7;
            Q7=makeQuery(id+"F3.opExtrude","SWEPT_BODY",BODY,{"disambiguationData":[OSD([sQuery(id+"F2.wireOp",EDGE,"E145.37"),sQuery(id+"F2.wireOp",EDGE,"E145.55"),sQuery(id+"F2.wireOp",EDGE,"E145.61"),sQuery(id+"F2.wireOp",EDGE,"E146")])]});
            booleanBodies(context, id + "F12", {"operationType" : BooleanOperationType.UNION, "tools" : qUnion([Q0, Q1, Q2, Q3, Q4, Q5, Q6, Q7])});
        }
    });
